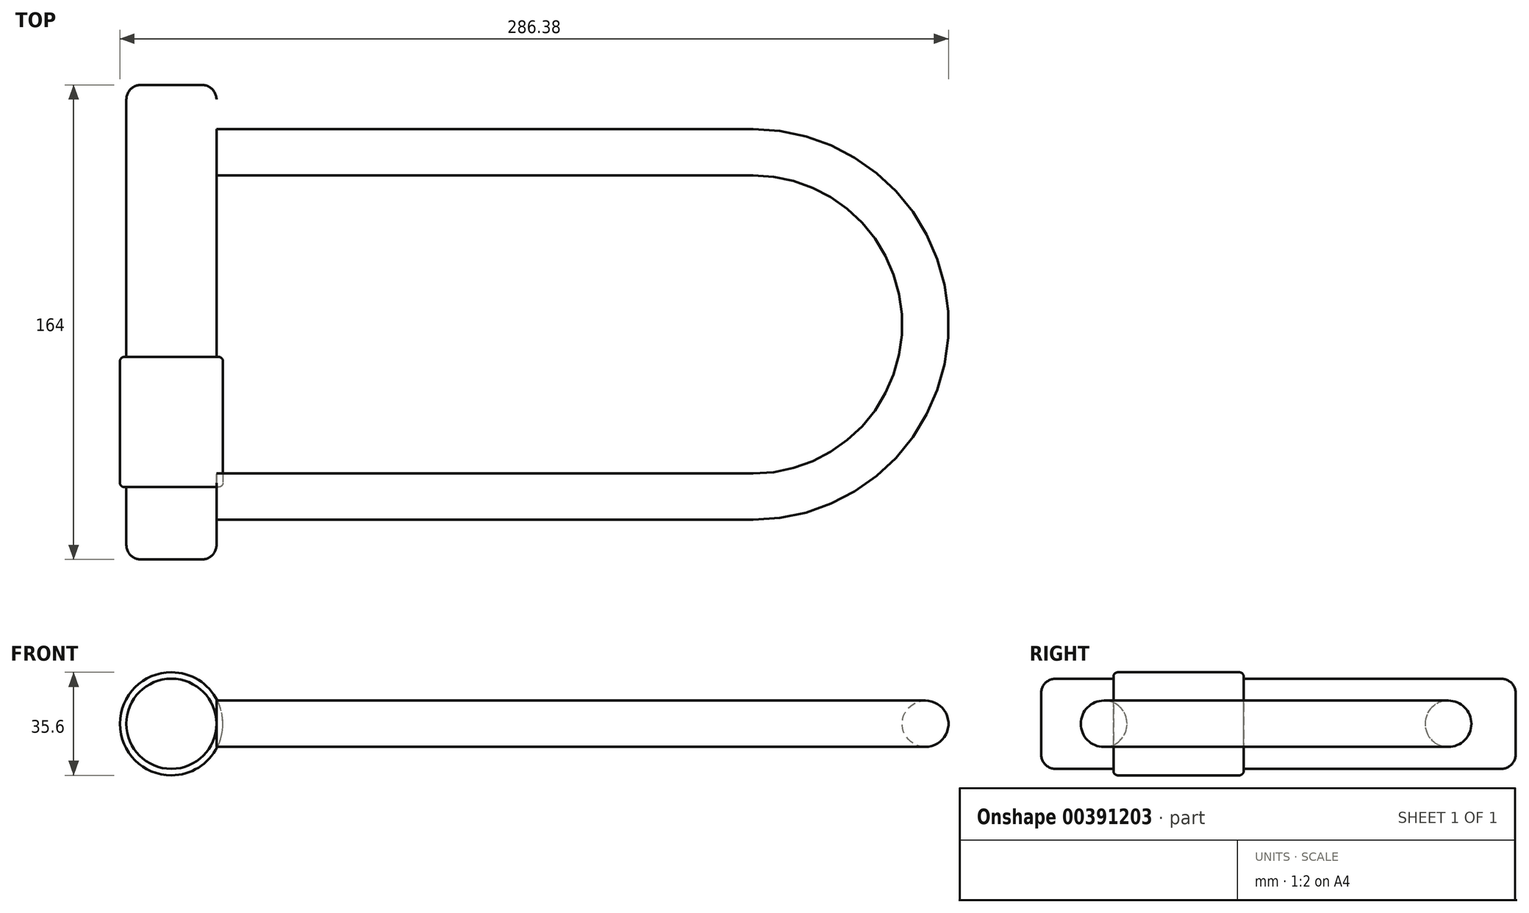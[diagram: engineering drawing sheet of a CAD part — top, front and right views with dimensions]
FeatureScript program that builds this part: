
annotation { "Feature Type Name" : "Feature", "Feature Type Description" : "" }
export const myFeature = defineFeature(function(context is Context, id is Id, definition is map)
    precondition{}
    {
        {
            var Q0;
            Q0=qCreatedBy(makeId("Top.planeOp"),FACE);
            var sketch = newSketch(context, id + "F0", { "sketchPlane" : qUnion([Q0])});
            skLineSegment(sketch, "E0", {"start": v(0, 0) * mm, "end": v(0, 164) * mm});
            skLineSegment(sketch, "E1", {"start": v(0, 164) * mm, "end": v(15.57, 164) * mm});
            skLineSegment(sketch, "E2", {"start": v(15.58, 164) * mm, "end": v(15.58, 70) * mm});
            skLineSegment(sketch, "E3", {"start": v(15.58, 70) * mm, "end": v(17.8, 70) * mm});
            skLineSegment(sketch, "E4", {"start": v(17.8, 70) * mm, "end": v(17.8, 25) * mm});
            skLineSegment(sketch, "E5", {"start": v(17.8, 25) * mm, "end": v(15.58, 25) * mm});
            skLineSegment(sketch, "E6", {"start": v(15.58, 25) * mm, "end": v(15.58, 0) * mm});
            skLineSegment(sketch, "E7", {"start": v(15.58, 0) * mm, "end": v(0, 0) * mm});
            skSolve(sketch);
        }
        {
            var Q0;
            Q0 = qSketchRegion(id + "F0", true);
            var Q1;
            Q1=sQuery(id+"F0.wireOp",EDGE,"E0");
            revolve(context, id + "F1", {"entities" : qUnion([Q0]), "axis" : qUnion([Q1]), "revolveType" : RevolveType.FULL});
        }
        {
            var Q0;
            Q0=makeQuery(id+"F1.opRevolve","SWEPT_EDGE",EDGE,{"disambiguationData":[OSD([sQuery(id+"F0.wireOp",EDGE,"E1"),sQuery(id+"F0.wireOp",EDGE,"E2")])]});
            var Q1;
            Q1=makeQuery(id+"F1.opRevolve","SWEPT_EDGE",EDGE,{"disambiguationData":[OSD([sQuery(id+"F0.wireOp",EDGE,"E6"),sQuery(id+"F0.wireOp",EDGE,"E7")])]});
            fillet(context, id + "F2", {"entities" : qUnion([Q0, Q1]), "radius" : 5 * mm, "tangentPropagation" : true, "allowEdgeOverflow" : false});
        }
        {
            var Q0;
            Q0=makeQuery(id+"F1.opRevolve","SWEPT_EDGE",EDGE,{"disambiguationData":[OSD([sQuery(id+"F0.wireOp",EDGE,"E3"),sQuery(id+"F0.wireOp",EDGE,"E4")])]});
            var Q1;
            Q1=makeQuery(id+"F1.opRevolve","SWEPT_EDGE",EDGE,{"disambiguationData":[OSD([sQuery(id+"F0.wireOp",EDGE,"E4"),sQuery(id+"F0.wireOp",EDGE,"E5")])]});
            fillet(context, id + "F3", {"entities" : qUnion([Q0, Q1]), "radius" : 1.5 * mm, "tangentPropagation" : true, "allowEdgeOverflow" : false});
        }
        {
            var Q0;
            Q0=qCreatedBy(makeId("Top.planeOp"),FACE);
            var sketch = newSketch(context, id + "F4", { "sketchPlane" : qUnion([Q0])});
            skLineSegment(sketch, "E8", {"start": v(15.57, 148.7) * mm, "end": v(15.57, 132.7) * mm, "construction": true});
            skLineSegment(sketch, "E9", {"start": v(15.57, 140.7) * mm, "end": v(201.08, 140.7) * mm});
            skArc(sketch, "E10", {"start": v(201.08, 140.7) * mm, "mid": v(260.58, 81.2) * mm, "end": v(201.08, 21.7) * mm});
            skLineSegment(sketch, "E11", {"start": v(201.08, 21.7) * mm, "end": v(15.57, 21.7) * mm});
            skLineSegment(sketch, "E12", {"start": v(15.57, 29.7) * mm, "end": v(15.58, 13.7) * mm, "construction": true});
            skPoint(sketch, "E13", {"position": v(260.57, 81.2) * mm});
            skSolve(sketch);
        }
        {
            var Q0;
            Q0=qCreatedBy(makeId("Right.planeOp"),FACE);
            var Q1;
            Q1=sQuery(id+"F4.wireOp",VERTEX,"E9.start");
            cPlane(context, id + "F5", {"entities" : qUnion([Q0, Q1]), "cplaneType" : CPlaneType.PLANE_POINT, "offset" : 25 * mm, "width" : 150 * mm, "height" : 150 * mm});
        }
        {
            var Q0;
            Q0=qCreatedBy(id+"F5.planeOp",FACE);
            var sketch = newSketch(context, id + "F6", { "sketchPlane" : qUnion([Q0])});
            skCircle(sketch, "E14", {"center": v(140.7, 0) * mm, "radius": 8 * mm});
            skSolve(sketch);
        }
        {
            var Q0;
            Q0=makeQuery(id+"F6.imprint","IMPRINT",FACE,{"disambiguationData":[TD([[makeQuery(id+"F6.imprint","IMPRINT",EDGE,{"derivedFrom":sQuery(id+"F6.wireOp",EDGE,"E14")}),1.0]])]});
            var Q1;
            Q1=sQuery(id+"F4.wireOp",EDGE,"E9");
            var Q2;
            Q2=sQuery(id+"F4.wireOp",EDGE,"E10");
            var Q3;
            Q3=sQuery(id+"F4.wireOp",EDGE,"E11");
            sweep(context, id + "F7", {"profiles" : qUnion([Q0]), "path" : qUnion([Q1, Q2, Q3])});
        }
    });
